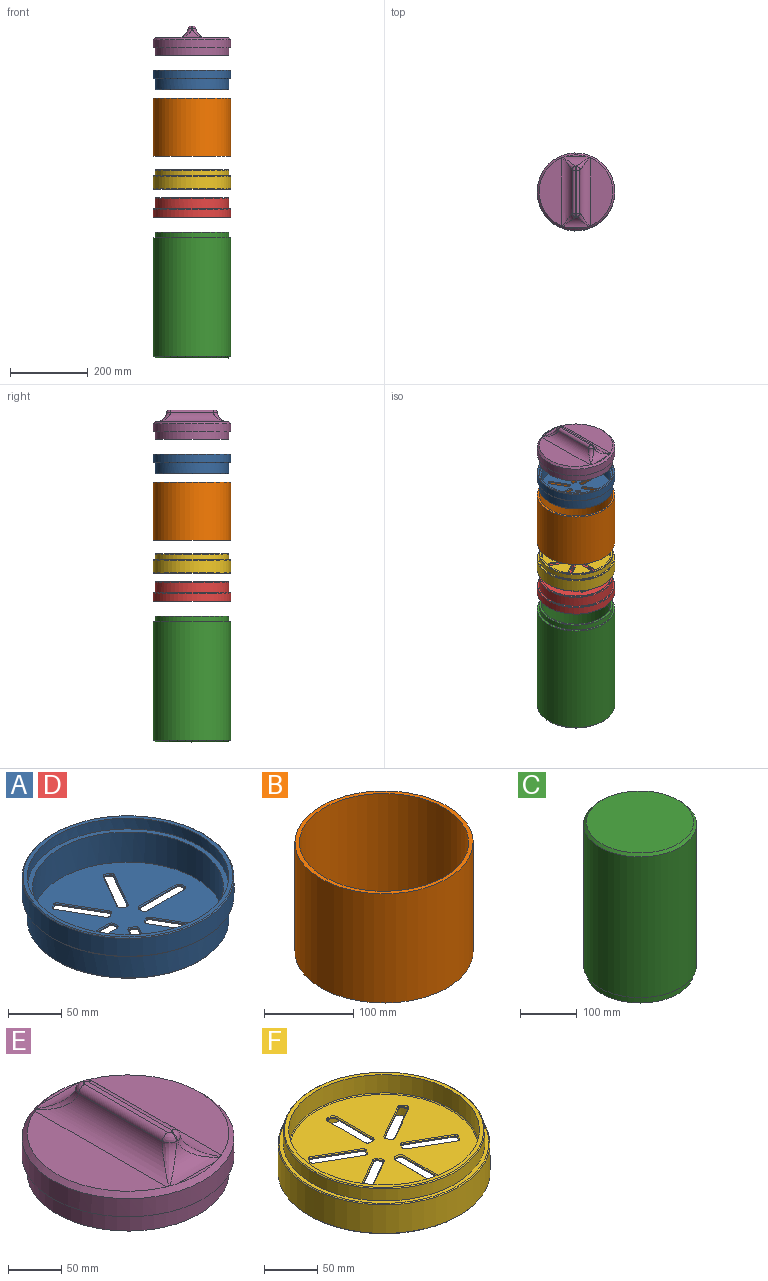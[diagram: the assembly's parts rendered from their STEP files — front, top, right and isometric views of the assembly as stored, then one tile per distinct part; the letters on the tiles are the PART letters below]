
ASSEMBLY  parts=6 mates=5
PART A: 158 faces, bbox 200x200x51.1 mm
  f0: cylinder r=95mm len=190mm, axis (0,0,-1), area 7341.9mm2, adj f1,f154
  f1: plane 198x198mm, normal (0,0,1), area 2437.9mm2, adj f0,f155
  f2: cylinder r=100mm len=200mm, axis (0,0,-1), area 12943.4mm2, adj f155,f156
  f3: plane 198x198mm, normal (0,0,-1), area 2437.9mm2, adj f4,f156
  f4: cylinder r=95mm len=190mm, axis (0,0,1), area 16414.8mm2, adj f3,f157
  f5: plane 42.94x25.37mm, normal (-0.61,-0.35,-0.71), area 69.3mm2, adj f6,f7,f27,f128
  f6: cone r=3mm half-angle=45deg, axis (0,0,-1), area 7.8mm2, adj f5,f8,f28,f128
  f7: cone r=3mm half-angle=45deg, axis (0,0,-1), area 7.8mm2, adj f5,f9,f26,f128
  f8: plane 3.1x2.37mm, normal (-0.35,0.61,-0.71), area 4.2mm2, adj f6,f10,f21,f128
  f9: plane 3.1x2.37mm, normal (0.35,-0.61,-0.71), area 4.2mm2, adj f7,f11,f25,f128
  f10: cone r=3mm half-angle=45deg, axis (0,0,-1), area 7.8mm2, adj f8,f12,f22,f128
  f11: cone r=3mm half-angle=45deg, axis (0,0,-1), area 7.8mm2, adj f9,f12,f24,f128
  f12: plane 42.94x25.37mm, normal (0.61,0.35,-0.71), area 69.3mm2, adj f10,f11,f23,f128
  f13: plane 42.94x25.37mm, normal (-0.61,-0.35,0.71), area 69.3mm2, adj f14,f15,f27,f129
  f14: cone r=3mm half-angle=45deg, axis (0,0,1), area 7.8mm2, adj f13,f16,f26,f129
  f15: cone r=3mm half-angle=45deg, axis (0,0,1), area 7.8mm2, adj f13,f17,f28,f129
  f16: plane 3.1x2.37mm, normal (0.35,-0.61,0.71), area 4.2mm2, adj f14,f18,f25,f129
  f17: plane 3.1x2.37mm, normal (-0.35,0.61,0.71), area 4.2mm2, adj f15,f19,f21,f129
  f18: cone r=3mm half-angle=45deg, axis (0,0,1), area 7.8mm2, adj f16,f20,f24,f129
  f19: cone r=3mm half-angle=45deg, axis (0,0,1), area 7.8mm2, adj f17,f20,f22,f129
  f20: plane 42.94x25.37mm, normal (0.61,0.35,0.71), area 69.3mm2, adj f18,f19,f23,f129
  f21: plane 2.6x1.5mm, normal (-0.5,0.87,0), area 3mm2, adj f8,f17,f22,f28
  f22: cylinder r=3mm len=4.1mm, axis (0,0,-1), area 4.7mm2, adj f10,f19,f21,f23
  f23: plane 42.44x24.5mm, normal (0.87,0.5,0), area 49mm2, adj f12,f20,f22,f24
  f24: cylinder r=3mm len=4.1mm, axis (0,0,-1), area 4.7mm2, adj f11,f18,f23,f25
  f25: plane 2.6x1.5mm, normal (0.5,-0.87,0), area 3mm2, adj f9,f16,f24,f26
  f26: cylinder r=3mm len=4.1mm, axis (0,0,-1), area 4.7mm2, adj f7,f14,f25,f27
  f27: plane 42.44x24.5mm, normal (-0.87,-0.5,0), area 49mm2, adj f5,f13,f26,f28
  f28: cylinder r=3mm len=4.1mm, axis (0,0,-1), area 4.7mm2, adj f6,f15,f21,f27
  f29: plane 42.94x25.37mm, normal (-0.61,0.35,-0.71), area 69.3mm2, adj f30,f31,f51,f128
  f30: cone r=3mm half-angle=45deg, axis (0,0,-1), area 7.8mm2, adj f29,f32,f52,f128
  f31: cone r=3mm half-angle=45deg, axis (0,0,-1), area 7.8mm2, adj f29,f33,f50,f128
  f32: plane 3.1x2.37mm, normal (0.35,0.61,-0.71), area 4.2mm2, adj f30,f34,f45,f128
  f33: plane 3.1x2.37mm, normal (-0.35,-0.61,-0.71), area 4.2mm2, adj f31,f35,f49,f128
  f34: cone r=3mm half-angle=45deg, axis (0,0,-1), area 7.8mm2, adj f32,f36,f46,f128
  f35: cone r=3mm half-angle=45deg, axis (0,0,-1), area 7.8mm2, adj f33,f36,f48,f128
  f36: plane 42.94x25.37mm, normal (0.61,-0.35,-0.71), area 69.3mm2, adj f34,f35,f47,f128
  f37: plane 42.94x25.37mm, normal (-0.61,0.35,0.71), area 69.3mm2, adj f38,f39,f51,f129
  f38: cone r=3mm half-angle=45deg, axis (0,0,1), area 7.8mm2, adj f37,f40,f50,f129
  f39: cone r=3mm half-angle=45deg, axis (0,0,1), area 7.8mm2, adj f37,f41,f52,f129
  f40: plane 3.1x2.37mm, normal (-0.35,-0.61,0.71), area 4.2mm2, adj f38,f42,f49,f129
  f41: plane 3.1x2.37mm, normal (0.35,0.61,0.71), area 4.2mm2, adj f39,f43,f45,f129
  f42: cone r=3mm half-angle=45deg, axis (0,0,1), area 7.8mm2, adj f40,f44,f48,f129
  f43: cone r=3mm half-angle=45deg, axis (0,0,1), area 7.8mm2, adj f41,f44,f46,f129
  f44: plane 42.94x25.37mm, normal (0.61,-0.35,0.71), area 69.3mm2, adj f42,f43,f47,f129
  f45: plane 2.6x1.5mm, normal (0.5,0.87,0), area 3mm2, adj f32,f41,f46,f52
  f46: cylinder r=3mm len=4.1mm, axis (0,0,-1), area 4.7mm2, adj f34,f43,f45,f47
  f47: plane 42.44x24.5mm, normal (0.87,-0.5,0), area 49mm2, adj f36,f44,f46,f48
  f48: cylinder r=3mm len=4.1mm, axis (0,0,-1), area 4.7mm2, adj f35,f42,f47,f49
  f49: plane 2.6x1.5mm, normal (-0.5,-0.87,0), area 3mm2, adj f33,f40,f48,f50
  f50: cylinder r=3mm len=4.1mm, axis (0,0,-1), area 4.7mm2, adj f31,f38,f49,f51
  f51: plane 42.44x24.5mm, normal (-0.87,0.5,0), area 49mm2, adj f29,f37,f50,f52
  f52: cylinder r=3mm len=4.1mm, axis (0,0,-1), area 4.7mm2, adj f30,f39,f45,f51
  f53: plane 49x1mm, normal (0,0.71,-0.71), area 69.3mm2, adj f54,f55,f75,f128
  f54: cone r=3mm half-angle=45deg, axis (0,0,-1), area 7.8mm2, adj f53,f56,f76,f128
  f55: cone r=3mm half-angle=45deg, axis (0,0,-1), area 7.8mm2, adj f53,f57,f74,f128
  f56: plane 3x1mm, normal (0.71,0,-0.71), area 4.2mm2, adj f54,f58,f69,f128
  f57: plane 3x1mm, normal (-0.71,0,-0.71), area 4.2mm2, adj f55,f59,f73,f128
  f58: cone r=3mm half-angle=45deg, axis (0,0,-1), area 7.8mm2, adj f56,f60,f70,f128
  f59: cone r=3mm half-angle=45deg, axis (0,0,-1), area 7.8mm2, adj f57,f60,f72,f128
  f60: plane 49x1mm, normal (0,-0.71,-0.71), area 69.3mm2, adj f58,f59,f71,f128
  f61: plane 49x1mm, normal (0,0.71,0.71), area 69.3mm2, adj f62,f63,f75,f129
  f62: cone r=3mm half-angle=45deg, axis (0,0,1), area 7.8mm2, adj f61,f64,f74,f129
  f63: cone r=3mm half-angle=45deg, axis (0,0,1), area 7.8mm2, adj f61,f65,f76,f129
  f64: plane 3x1mm, normal (-0.71,0,0.71), area 4.2mm2, adj f62,f66,f73,f129
  f65: plane 3x1mm, normal (0.71,0,0.71), area 4.2mm2, adj f63,f67,f69,f129
  f66: cone r=3mm half-angle=45deg, axis (0,0,1), area 7.8mm2, adj f64,f68,f72,f129
  f67: cone r=3mm half-angle=45deg, axis (0,0,1), area 7.8mm2, adj f65,f68,f70,f129
  f68: plane 49x1mm, normal (0,-0.71,0.71), area 69.3mm2, adj f66,f67,f71,f129
  f69: plane 3x1mm, normal (1,0,0), area 3mm2, adj f56,f65,f70,f76
  f70: cylinder r=3mm len=3mm, axis (0,0,-1), area 4.7mm2, adj f58,f67,f69,f71
  f71: plane 49x1mm, normal (0,-1,0), area 49mm2, adj f60,f68,f70,f72
  f72: cylinder r=3mm len=3mm, axis (0,0,-1), area 4.7mm2, adj f59,f66,f71,f73
  f73: plane 3x1mm, normal (-1,0,0), area 3mm2, adj f57,f64,f72,f74
  f74: cylinder r=3mm len=3mm, axis (0,0,-1), area 4.7mm2, adj f55,f62,f73,f75
  f75: plane 49x1mm, normal (0,1,0), area 49mm2, adj f53,f61,f74,f76
  f76: cylinder r=3mm len=3mm, axis (0,0,-1), area 4.7mm2, adj f54,f63,f69,f75
  f77: plane 42.94x25.37mm, normal (0.61,0.35,-0.71), area 69.3mm2, adj f78,f79,f99,f128
  f78: cone r=3mm half-angle=45deg, axis (0,0,-1), area 7.8mm2, adj f77,f80,f100,f128
  f79: cone r=3mm half-angle=45deg, axis (0,0,-1), area 7.8mm2, adj f77,f81,f98,f128
  f80: plane 3.1x2.37mm, normal (0.35,-0.61,-0.71), area 4.2mm2, adj f78,f82,f93,f128
  f81: plane 3.1x2.37mm, normal (-0.35,0.61,-0.71), area 4.2mm2, adj f79,f83,f97,f128
  f82: cone r=3mm half-angle=45deg, axis (0,0,-1), area 7.8mm2, adj f80,f84,f94,f128
  f83: cone r=3mm half-angle=45deg, axis (0,0,-1), area 7.8mm2, adj f81,f84,f96,f128
  f84: plane 42.94x25.37mm, normal (-0.61,-0.35,-0.71), area 69.3mm2, adj f82,f83,f95,f128
  f85: plane 42.94x25.37mm, normal (0.61,0.35,0.71), area 69.3mm2, adj f86,f87,f99,f129
  f86: cone r=3mm half-angle=45deg, axis (0,0,1), area 7.8mm2, adj f85,f88,f98,f129
  f87: cone r=3mm half-angle=45deg, axis (0,0,1), area 7.8mm2, adj f85,f89,f100,f129
  f88: plane 3.1x2.37mm, normal (-0.35,0.61,0.71), area 4.2mm2, adj f86,f90,f97,f129
  f89: plane 3.1x2.37mm, normal (0.35,-0.61,0.71), area 4.2mm2, adj f87,f91,f93,f129
  f90: cone r=3mm half-angle=45deg, axis (0,0,1), area 7.8mm2, adj f88,f92,f96,f129
  f91: cone r=3mm half-angle=45deg, axis (0,0,1), area 7.8mm2, adj f89,f92,f94,f129
  f92: plane 42.94x25.37mm, normal (-0.61,-0.35,0.71), area 69.3mm2, adj f90,f91,f95,f129
  f93: plane 2.6x1.5mm, normal (0.5,-0.87,0), area 3mm2, adj f80,f89,f94,f100
  f94: cylinder r=3mm len=4.1mm, axis (0,0,-1), area 4.7mm2, adj f82,f91,f93,f95
  f95: plane 42.44x24.5mm, normal (-0.87,-0.5,0), area 49mm2, adj f84,f92,f94,f96
  f96: cylinder r=3mm len=4.1mm, axis (0,0,-1), area 4.7mm2, adj f83,f90,f95,f97
  f97: plane 2.6x1.5mm, normal (-0.5,0.87,0), area 3mm2, adj f81,f88,f96,f98
  f98: cylinder r=3mm len=4.1mm, axis (0,0,-1), area 4.7mm2, adj f79,f86,f97,f99
  f99: plane 42.44x24.5mm, normal (0.87,0.5,0), area 49mm2, adj f77,f85,f98,f100
  f100: cylinder r=3mm len=4.1mm, axis (0,0,-1), area 4.7mm2, adj f78,f87,f93,f99
  f101: plane 42.94x25.37mm, normal (0.61,-0.35,-0.71), area 69.3mm2, adj f102,f103,f123,f128
  f102: cone r=3mm half-angle=45deg, axis (0,0,-1), area 7.8mm2, adj f101,f104,f124,f128
  f103: cone r=3mm half-angle=45deg, axis (0,0,-1), area 7.8mm2, adj f101,f105,f122,f128
  f104: plane 3.1x2.37mm, normal (-0.35,-0.61,-0.71), area 4.2mm2, adj f102,f106,f117,f128
  f105: plane 3.1x2.37mm, normal (0.35,0.61,-0.71), area 4.2mm2, adj f103,f107,f121,f128
  f106: cone r=3mm half-angle=45deg, axis (0,0,-1), area 7.8mm2, adj f104,f108,f118,f128
  f107: cone r=3mm half-angle=45deg, axis (0,0,-1), area 7.8mm2, adj f105,f108,f120,f128
  f108: plane 42.94x25.37mm, normal (-0.61,0.35,-0.71), area 69.3mm2, adj f106,f107,f119,f128
  f109: plane 42.94x25.37mm, normal (0.61,-0.35,0.71), area 69.3mm2, adj f110,f111,f123,f129
  f110: cone r=3mm half-angle=45deg, axis (0,0,1), area 7.8mm2, adj f109,f112,f122,f129
  f111: cone r=3mm half-angle=45deg, axis (0,0,1), area 7.8mm2, adj f109,f113,f124,f129
  f112: plane 3.1x2.37mm, normal (0.35,0.61,0.71), area 4.2mm2, adj f110,f114,f121,f129
  f113: plane 3.1x2.37mm, normal (-0.35,-0.61,0.71), area 4.2mm2, adj f111,f115,f117,f129
  f114: cone r=3mm half-angle=45deg, axis (0,0,1), area 7.8mm2, adj f112,f116,f120,f129
  f115: cone r=3mm half-angle=45deg, axis (0,0,1), area 7.8mm2, adj f113,f116,f118,f129
  f116: plane 42.94x25.37mm, normal (-0.61,0.35,0.71), area 69.3mm2, adj f114,f115,f119,f129
  f117: plane 2.6x1.5mm, normal (-0.5,-0.87,0), area 3mm2, adj f104,f113,f118,f124
  f118: cylinder r=3mm len=4.1mm, axis (0,0,-1), area 4.7mm2, adj f106,f115,f117,f119
  f119: plane 42.44x24.5mm, normal (-0.87,0.5,0), area 49mm2, adj f108,f116,f118,f120
  f120: cylinder r=3mm len=4.1mm, axis (0,0,-1), area 4.7mm2, adj f107,f114,f119,f121
  f121: plane 2.6x1.5mm, normal (0.5,0.87,0), area 3mm2, adj f105,f112,f120,f122
  f122: cylinder r=3mm len=4.1mm, axis (0,0,-1), area 4.7mm2, adj f103,f110,f121,f123
  f123: plane 42.44x24.5mm, normal (0.87,-0.5,0), area 49mm2, adj f101,f109,f122,f124
  f124: cylinder r=3mm len=4.1mm, axis (0,0,-1), area 4.7mm2, adj f102,f111,f117,f123
  f125: cylinder r=90mm len=180mm, axis (0,0,1), area 565.5mm2, adj f127,f128
  f126: cylinder r=90mm len=180mm, axis (0,0,1), area 19678.9mm2, adj f129,f154
  f127: plane 188x188mm, normal (0,0,-1), area 2312.2mm2, adj f125,f157
  f128: plane 180x180mm, normal (0,0,-1), area 21767.3mm2, adj f5,f6,f7,f8,f9,f10,f11,f12
  f129: plane 180x180mm, normal (0,0,1), area 21767.3mm2, adj f13,f14,f15,f16,f17,f18,f19,f20
  f130: plane 3x1mm, normal (1,0,0), area 3mm2, adj f131,f137,f141,f150
  f131: cylinder r=3mm len=3mm, axis (0,0,-1), area 4.7mm2, adj f130,f132,f139,f148
  f132: plane 49x1mm, normal (0,-1,0), area 49mm2, adj f131,f133,f138,f146
  f133: cylinder r=3mm len=3mm, axis (0,0,-1), area 4.7mm2, adj f132,f134,f140,f147
  f134: plane 3x1mm, normal (-1,0,0), area 3mm2, adj f133,f135,f142,f149
  f135: cylinder r=3mm len=3mm, axis (0,0,-1), area 4.7mm2, adj f134,f136,f144,f151
  f136: plane 49x1mm, normal (0,1,0), area 49mm2, adj f135,f137,f145,f153
  f137: cylinder r=3mm len=3mm, axis (0,0,-1), area 4.7mm2, adj f130,f136,f143,f152
  f138: plane 49x1mm, normal (0,-0.71,0.71), area 69.3mm2, adj f129,f132,f139,f140
  f139: cone r=3mm half-angle=45deg, axis (0,0,1), area 7.8mm2, adj f129,f131,f138,f141
  f140: cone r=3mm half-angle=45deg, axis (0,0,1), area 7.8mm2, adj f129,f133,f138,f142
  f141: plane 3x1mm, normal (0.71,0,0.71), area 4.2mm2, adj f129,f130,f139,f143
  f142: plane 3x1mm, normal (-0.71,0,0.71), area 4.2mm2, adj f129,f134,f140,f144
  f143: cone r=3mm half-angle=45deg, axis (0,0,1), area 7.8mm2, adj f129,f137,f141,f145
  f144: cone r=3mm half-angle=45deg, axis (0,0,1), area 7.8mm2, adj f129,f135,f142,f145
  f145: plane 49x1mm, normal (0,0.71,0.71), area 69.3mm2, adj f129,f136,f143,f144
  f146: plane 49x1mm, normal (0,-0.71,-0.71), area 69.3mm2, adj f128,f132,f147,f148
  f147: cone r=3mm half-angle=45deg, axis (0,0,-1), area 7.8mm2, adj f128,f133,f146,f149
  f148: cone r=3mm half-angle=45deg, axis (0,0,-1), area 7.8mm2, adj f128,f131,f146,f150
  f149: plane 3x1mm, normal (-0.71,0,-0.71), area 4.2mm2, adj f128,f134,f147,f151
  f150: plane 3x1mm, normal (0.71,0,-0.71), area 4.2mm2, adj f128,f130,f148,f152
  f151: cone r=3mm half-angle=45deg, axis (0,0,-1), area 7.8mm2, adj f128,f135,f149,f153
  f152: cone r=3mm half-angle=45deg, axis (0,0,-1), area 7.8mm2, adj f128,f137,f150,f153
  f153: plane 49x1mm, normal (0,0.71,-0.71), area 69.3mm2, adj f128,f136,f151,f152
  f154: plane 190x190mm, normal (0,0,1), area 2906mm2, adj f0,f126
  f155: cone r=99mm half-angle=45deg, axis (0,0,-1), area 884.1mm2, adj f1,f2
  f156: cone r=100mm half-angle=45deg, axis (0,0,1), area 884.1mm2, adj f2,f3
  f157: cone r=95mm half-angle=45deg, axis (0,0,1), area 839.7mm2, adj f4,f127
PART B: 4 faces, bbox 200x200x150 mm
  f0: cylinder r=95mm len=190mm, axis (0,0,-1), area 89535.4mm2, adj f2,f3
  f1: cylinder r=100mm len=200mm, axis (0,0,-1), area 94247.8mm2, adj f2,f3
  f2: plane 200x200mm, normal (0,0,1), area 3063.1mm2, adj f0,f1
  f3: plane 200x200mm, normal (0,0,-1), area 3063.1mm2, adj f0,f1
PART C: 10 faces, bbox 200x200x325 mm
  f0: cylinder r=95mm len=190mm, axis (0,0,1), area 8953.5mm2, adj f3,f6
  f1: cylinder r=95mm len=290mm, axis (0,0,-1), area 173101.8mm2, adj f4,f5
  f2: cylinder r=90mm len=180mm, axis (0,0,1), area 16964.6mm2, adj f3,f4
  f3: plane 190x190mm, normal (0,0,-1), area 2906mm2, adj f0,f2
  f4: plane 190x190mm, normal (0,0,1), area 2906mm2, adj f1,f2
  f5: plane 190x190mm, normal (0,0,-1), area 28352.9mm2, adj f1
  f6: plane 200x200mm, normal (0,0,-1), area 3063.1mm2, adj f0,f9
  f7: plane 190x190mm, normal (0,0,1), area 28352.9mm2, adj f8
  f8: cone r=95mm half-angle=45deg, axis (0,0,-1), area 4331.8mm2, adj f7,f9
  f9: cylinder r=100mm len=305mm, axis (0,0,-1), area 191637.2mm2, adj f6,f8
PART D: same geometry as A
PART E: 30 faces, bbox 200x200x76 mm
  f0: plane 50.69x3.44mm, normal (0,0,1), area 116.8mm2, adj f12,f17
  f1: plane 175.37x58.44mm, normal (0,0,1), area 7406.2mm2, adj f12,f15
  f2: plane 50.69x3.44mm, normal (0,0,1), area 116.8mm2, adj f12,f14
  f3: plane 175.37x58.44mm, normal (0,0,1), area 7406.2mm2, adj f12,f16
  f4: cylinder r=95mm len=190mm, axis (0,0,-1), area 6565.9mm2, adj f10,f11
  f5: cylinder r=100mm len=200mm, axis (0,0,-1), area 13194.7mm2, adj f6,f12
  f6: plane 200x200mm, normal (0,0,-1), area 3063.1mm2, adj f5,f7
  f7: cylinder r=95mm len=190mm, axis (0,0,1), area 11938.1mm2, adj f6,f9
  f8: cylinder r=90mm len=180mm, axis (0,0,1), area 16964.6mm2, adj f9,f10
  f9: plane 190x190mm, normal (0,0,-1), area 2906mm2, adj f7,f8
  f10: plane 190x190mm, normal (0,0,1), area 2906mm2, adj f4,f8
  f11: plane 190x190mm, normal (0,0,-1), area 28352.9mm2, adj f4
  f12: cone r=95mm half-angle=45deg, axis (0,0,-1), area 4336.3mm2, adj f0,f1,f2,f3,f5,f14,f15,f16
  f13: plane 115.09x5.09mm, normal (0,0,1), area 582.2mm2, adj f22,f23,f24,f25,f26,f27,f28,f29
  f14: cylinder r=26.56mm len=66mm, axis (-1,0,0), area 1094.3mm2, adj f2,f12,f18,f21,f25
  f15: cylinder r=26.56mm len=176.97mm, axis (0,-1,0), area 5337.6mm2, adj f1,f12,f18,f19,f29
  f16: cylinder r=26.56mm len=176.97mm, axis (0,1,0), area 5337.6mm2, adj f3,f12,f20,f21,f22
  f17: cylinder r=26.56mm len=66mm, axis (1,0,0), area 1094.3mm2, adj f0,f12,f19,f20,f26
  f18: bspline ~36.16x36.16mm, area 410.2mm2, adj f12,f14,f15,f27
  f19: bspline ~36.16x36.16mm, area 410.2mm2, adj f12,f15,f17,f28
  f20: bspline ~36.16x36.16mm, area 410.2mm2, adj f12,f16,f17,f24
  f21: bspline ~36.16x36.16mm, area 410.2mm2, adj f12,f14,f16,f23
  f22: cylinder r=7.73mm len=111.25mm, axis (0,1,0), area 1242.4mm2, adj f13,f16,f23,f24
  f23: bspline ~10.64x10.11mm, area 111.5mm2, adj f13,f21,f22,f25
  f24: bspline ~10.64x10.11mm, area 111.5mm2, adj f13,f20,f22,f26
  f25: cylinder r=7.73mm len=7.67mm, axis (-1,0,0), area 14mm2, adj f13,f14,f23,f27
  f26: cylinder r=7.73mm len=7.67mm, axis (1,0,0), area 14mm2, adj f13,f17,f24,f28
  f27: bspline ~10.64x10.11mm, area 111.5mm2, adj f13,f18,f25,f29
  f28: bspline ~10.64x10.11mm, area 111.5mm2, adj f13,f19,f26,f29
  f29: cylinder r=7.73mm len=111.25mm, axis (0,-1,0), area 1242.4mm2, adj f13,f15,f27,f28
PART F: 158 faces, bbox 200x200x50 mm
  f0: plane 2.6x1.5mm, normal (-0.87,0.5,0), area 3mm2, adj f1,f7,f59,f104
  f1: cylinder r=3mm len=4.1mm, axis (0,0,1), area 4.7mm2, adj f0,f2,f61,f105
  f2: plane 42.44x24.5mm, normal (-0.5,-0.87,0), area 49mm2, adj f1,f3,f63,f107
  f3: cylinder r=3mm len=4.1mm, axis (0,0,1), area 4.7mm2, adj f2,f4,f62,f109
  f4: plane 2.6x1.5mm, normal (0.87,-0.5,0), area 3mm2, adj f3,f5,f60,f111
  f5: cylinder r=3mm len=4.1mm, axis (0,0,1), area 4.7mm2, adj f4,f6,f58,f110
  f6: plane 42.44x24.5mm, normal (0.5,0.87,0), area 49mm2, adj f5,f7,f56,f108
  f7: cylinder r=3mm len=4.1mm, axis (0,0,1), area 4.7mm2, adj f0,f6,f57,f106
  f8: plane 2.6x1.5mm, normal (-0.87,-0.5,0), area 3mm2, adj f9,f15,f99,f112
  f9: cylinder r=3mm len=4.1mm, axis (0,0,1), area 4.7mm2, adj f8,f10,f101,f113
  f10: plane 42.44x24.5mm, normal (0.5,-0.87,0), area 49mm2, adj f9,f11,f103,f115
  f11: cylinder r=3mm len=4.1mm, axis (0,0,1), area 4.7mm2, adj f10,f12,f102,f117
  f12: plane 2.6x1.5mm, normal (0.87,0.5,0), area 3mm2, adj f11,f13,f100,f119
  f13: cylinder r=3mm len=4.1mm, axis (0,0,1), area 4.7mm2, adj f12,f14,f98,f118
  f14: plane 42.44x24.5mm, normal (-0.5,0.87,0), area 49mm2, adj f13,f15,f96,f116
  f15: cylinder r=3mm len=4.1mm, axis (0,0,1), area 4.7mm2, adj f8,f14,f97,f114
  f16: plane 3x1mm, normal (0,-1,0), area 3mm2, adj f17,f23,f91,f123
  f17: cylinder r=3mm len=3mm, axis (0,0,1), area 4.7mm2, adj f16,f18,f89,f125
  f18: plane 49x1mm, normal (1,0,0), area 49mm2, adj f17,f19,f88,f127
  f19: cylinder r=3mm len=3mm, axis (0,0,1), area 4.7mm2, adj f18,f20,f90,f126
  f20: plane 3x1mm, normal (0,1,0), area 3mm2, adj f19,f21,f92,f124
  f21: cylinder r=3mm len=3mm, axis (0,0,1), area 4.7mm2, adj f20,f22,f94,f122
  f22: plane 49x1mm, normal (-1,0,0), area 49mm2, adj f21,f23,f95,f120
  f23: cylinder r=3mm len=3mm, axis (0,0,1), area 4.7mm2, adj f16,f22,f93,f121
  f24: plane 2.6x1.5mm, normal (0.87,-0.5,0), area 3mm2, adj f25,f31,f83,f131
  f25: cylinder r=3mm len=4.1mm, axis (0,0,1), area 4.7mm2, adj f24,f26,f81,f133
  f26: plane 42.44x24.5mm, normal (0.5,0.87,0), area 49mm2, adj f25,f27,f80,f135
  f27: cylinder r=3mm len=4.1mm, axis (0,0,1), area 4.7mm2, adj f26,f28,f82,f134
  f28: plane 2.6x1.5mm, normal (-0.87,0.5,0), area 3mm2, adj f27,f29,f84,f132
  f29: cylinder r=3mm len=4.1mm, axis (0,0,1), area 4.7mm2, adj f28,f30,f86,f130
  f30: plane 42.44x24.5mm, normal (-0.5,-0.87,0), area 49mm2, adj f29,f31,f87,f128
  f31: cylinder r=3mm len=4.1mm, axis (0,0,1), area 4.7mm2, adj f24,f30,f85,f129
  f32: plane 2.6x1.5mm, normal (0.87,0.5,0), area 3mm2, adj f33,f39,f75,f139
  f33: cylinder r=3mm len=4.1mm, axis (0,0,1), area 4.7mm2, adj f32,f34,f73,f141
  f34: plane 42.44x24.5mm, normal (-0.5,0.87,0), area 49mm2, adj f33,f35,f72,f143
  f35: cylinder r=3mm len=4.1mm, axis (0,0,1), area 4.7mm2, adj f34,f36,f74,f142
  f36: plane 2.6x1.5mm, normal (-0.87,-0.5,0), area 3mm2, adj f35,f37,f76,f140
  f37: cylinder r=3mm len=4.1mm, axis (0,0,1), area 4.7mm2, adj f36,f38,f78,f138
  f38: plane 42.44x24.5mm, normal (0.5,-0.87,0), area 49mm2, adj f37,f39,f79,f136
  f39: cylinder r=3mm len=4.1mm, axis (0,0,1), area 4.7mm2, adj f32,f38,f77,f137
  f40: plane 188x188mm, normal (0,0,-1), area 24079.5mm2, adj f56,f57,f58,f59,f60,f61,f62,f63
  f41: cylinder r=100mm len=200mm, axis (0,0,-1), area 20734.5mm2, adj f155,f157
  f42: plane 198x198mm, normal (0,0,1), area 2437.9mm2, adj f44,f157
  f43: cylinder r=90mm len=180mm, axis (0,0,-1), area 11875.2mm2, adj f45,f152
  f44: cylinder r=95mm len=190mm, axis (0,0,-1), area 8356.6mm2, adj f42,f156
  f45: plane 188x188mm, normal (0,0,1), area 2312.2mm2, adj f43,f156
  f46: cylinder r=95mm len=190mm, axis (0,0,1), area 14325.7mm2, adj f153,f154
  f47: plane 178x178mm, normal (0,0,1), area 21205mm2, adj f104,f105,f106,f107,f108,f109,f110,f111
  f48: plane 3x1mm, normal (0,-1,0), area 3mm2, adj f49,f55,f71,f148
  f49: cylinder r=3mm len=3mm, axis (0,0,1), area 4.7mm2, adj f48,f50,f70,f150
  f50: plane 49x1mm, normal (1,0,0), area 49mm2, adj f49,f51,f68,f151
  f51: cylinder r=3mm len=3mm, axis (0,0,1), area 4.7mm2, adj f50,f52,f66,f149
  f52: plane 3x1mm, normal (0,1,0), area 3mm2, adj f51,f53,f64,f147
  f53: cylinder r=3mm len=3mm, axis (0,0,1), area 4.7mm2, adj f52,f54,f65,f145
  f54: plane 49x1mm, normal (-1,0,0), area 49mm2, adj f53,f55,f67,f144
  f55: cylinder r=3mm len=3mm, axis (0,0,1), area 4.7mm2, adj f48,f54,f69,f146
  f56: plane 42.94x25.37mm, normal (0.35,0.61,-0.71), area 69.3mm2, adj f6,f40,f57,f58
  f57: cone r=4mm half-angle=45deg, axis (0,0,-1), area 7.8mm2, adj f7,f40,f56,f59
  f58: cone r=4mm half-angle=45deg, axis (0,0,-1), area 7.8mm2, adj f5,f40,f56,f60
  f59: plane 3.1x2.37mm, normal (-0.61,0.35,-0.71), area 4.2mm2, adj f0,f40,f57,f61
  f60: plane 3.1x2.37mm, normal (0.61,-0.35,-0.71), area 4.2mm2, adj f4,f40,f58,f62
  f61: cone r=4mm half-angle=45deg, axis (0,0,-1), area 7.8mm2, adj f1,f40,f59,f63
  f62: cone r=4mm half-angle=45deg, axis (0,0,-1), area 7.8mm2, adj f3,f40,f60,f63
  f63: plane 42.94x25.37mm, normal (-0.35,-0.61,-0.71), area 69.3mm2, adj f2,f40,f61,f62
  f64: plane 3x1mm, normal (0,0.71,-0.71), area 4.2mm2, adj f40,f52,f65,f66
  f65: cone r=4mm half-angle=45deg, axis (0,0,-1), area 7.8mm2, adj f40,f53,f64,f67
  f66: cone r=4mm half-angle=45deg, axis (0,0,-1), area 7.8mm2, adj f40,f51,f64,f68
  f67: plane 49x1mm, normal (-0.71,0,-0.71), area 69.3mm2, adj f40,f54,f65,f69
  f68: plane 49x1mm, normal (0.71,0,-0.71), area 69.3mm2, adj f40,f50,f66,f70
  f69: cone r=4mm half-angle=45deg, axis (0,0,-1), area 7.8mm2, adj f40,f55,f67,f71
  f70: cone r=4mm half-angle=45deg, axis (0,0,-1), area 7.8mm2, adj f40,f49,f68,f71
  f71: plane 3x1mm, normal (0,-0.71,-0.71), area 4.2mm2, adj f40,f48,f69,f70
  f72: plane 42.94x25.37mm, normal (-0.35,0.61,-0.71), area 69.3mm2, adj f34,f40,f73,f74
  f73: cone r=4mm half-angle=45deg, axis (0,0,-1), area 7.8mm2, adj f33,f40,f72,f75
  f74: cone r=4mm half-angle=45deg, axis (0,0,-1), area 7.8mm2, adj f35,f40,f72,f76
  f75: plane 3.1x2.37mm, normal (0.61,0.35,-0.71), area 4.2mm2, adj f32,f40,f73,f77
  f76: plane 3.1x2.37mm, normal (-0.61,-0.35,-0.71), area 4.2mm2, adj f36,f40,f74,f78
  f77: cone r=4mm half-angle=45deg, axis (0,0,-1), area 7.8mm2, adj f39,f40,f75,f79
  f78: cone r=4mm half-angle=45deg, axis (0,0,-1), area 7.8mm2, adj f37,f40,f76,f79
  f79: plane 42.94x25.37mm, normal (0.35,-0.61,-0.71), area 69.3mm2, adj f38,f40,f77,f78
  f80: plane 42.94x25.37mm, normal (0.35,0.61,-0.71), area 69.3mm2, adj f26,f40,f81,f82
  f81: cone r=4mm half-angle=45deg, axis (0,0,-1), area 7.8mm2, adj f25,f40,f80,f83
  f82: cone r=4mm half-angle=45deg, axis (0,0,-1), area 7.8mm2, adj f27,f40,f80,f84
  f83: plane 3.1x2.37mm, normal (0.61,-0.35,-0.71), area 4.2mm2, adj f24,f40,f81,f85
  f84: plane 3.1x2.37mm, normal (-0.61,0.35,-0.71), area 4.2mm2, adj f28,f40,f82,f86
  f85: cone r=4mm half-angle=45deg, axis (0,0,-1), area 7.8mm2, adj f31,f40,f83,f87
  f86: cone r=4mm half-angle=45deg, axis (0,0,-1), area 7.8mm2, adj f29,f40,f84,f87
  f87: plane 42.94x25.37mm, normal (-0.35,-0.61,-0.71), area 69.3mm2, adj f30,f40,f85,f86
  f88: plane 49x1mm, normal (0.71,0,-0.71), area 69.3mm2, adj f18,f40,f89,f90
  f89: cone r=4mm half-angle=45deg, axis (0,0,-1), area 7.8mm2, adj f17,f40,f88,f91
  f90: cone r=4mm half-angle=45deg, axis (0,0,-1), area 7.8mm2, adj f19,f40,f88,f92
  f91: plane 3x1mm, normal (0,-0.71,-0.71), area 4.2mm2, adj f16,f40,f89,f93
  f92: plane 3x1mm, normal (0,0.71,-0.71), area 4.2mm2, adj f20,f40,f90,f94
  f93: cone r=4mm half-angle=45deg, axis (0,0,-1), area 7.8mm2, adj f23,f40,f91,f95
  f94: cone r=4mm half-angle=45deg, axis (0,0,-1), area 7.8mm2, adj f21,f40,f92,f95
  f95: plane 49x1mm, normal (-0.71,0,-0.71), area 69.3mm2, adj f22,f40,f93,f94
  f96: plane 42.94x25.37mm, normal (-0.35,0.61,-0.71), area 69.3mm2, adj f14,f40,f97,f98
  f97: cone r=4mm half-angle=45deg, axis (0,0,-1), area 7.8mm2, adj f15,f40,f96,f99
  f98: cone r=4mm half-angle=45deg, axis (0,0,-1), area 7.8mm2, adj f13,f40,f96,f100
  f99: plane 3.1x2.37mm, normal (-0.61,-0.35,-0.71), area 4.2mm2, adj f8,f40,f97,f101
  f100: plane 3.1x2.37mm, normal (0.61,0.35,-0.71), area 4.2mm2, adj f12,f40,f98,f102
  f101: cone r=4mm half-angle=45deg, axis (0,0,-1), area 7.8mm2, adj f9,f40,f99,f103
  f102: cone r=4mm half-angle=45deg, axis (0,0,-1), area 7.8mm2, adj f11,f40,f100,f103
  f103: plane 42.94x25.37mm, normal (0.35,-0.61,-0.71), area 69.3mm2, adj f10,f40,f101,f102
  f104: plane 3.1x2.37mm, normal (-0.61,0.35,0.71), area 4.2mm2, adj f0,f47,f105,f106
  f105: cone r=3mm half-angle=45deg, axis (0,0,1), area 7.8mm2, adj f1,f47,f104,f107
  f106: cone r=3mm half-angle=45deg, axis (0,0,1), area 7.8mm2, adj f7,f47,f104,f108
  f107: plane 42.94x25.37mm, normal (-0.35,-0.61,0.71), area 69.3mm2, adj f2,f47,f105,f109
  f108: plane 42.94x25.37mm, normal (0.35,0.61,0.71), area 69.3mm2, adj f6,f47,f106,f110
  f109: cone r=3mm half-angle=45deg, axis (0,0,1), area 7.8mm2, adj f3,f47,f107,f111
  f110: cone r=3mm half-angle=45deg, axis (0,0,1), area 7.8mm2, adj f5,f47,f108,f111
  f111: plane 3.1x2.37mm, normal (0.61,-0.35,0.71), area 4.2mm2, adj f4,f47,f109,f110
  f112: plane 3.1x2.37mm, normal (-0.61,-0.35,0.71), area 4.2mm2, adj f8,f47,f113,f114
  f113: cone r=3mm half-angle=45deg, axis (0,0,1), area 7.8mm2, adj f9,f47,f112,f115
  f114: cone r=3mm half-angle=45deg, axis (0,0,1), area 7.8mm2, adj f15,f47,f112,f116
  f115: plane 42.94x25.37mm, normal (0.35,-0.61,0.71), area 69.3mm2, adj f10,f47,f113,f117
  f116: plane 42.94x25.37mm, normal (-0.35,0.61,0.71), area 69.3mm2, adj f14,f47,f114,f118
  f117: cone r=3mm half-angle=45deg, axis (0,0,1), area 7.8mm2, adj f11,f47,f115,f119
  f118: cone r=3mm half-angle=45deg, axis (0,0,1), area 7.8mm2, adj f13,f47,f116,f119
  f119: plane 3.1x2.37mm, normal (0.61,0.35,0.71), area 4.2mm2, adj f12,f47,f117,f118
  f120: plane 49x1mm, normal (-0.71,0,0.71), area 69.3mm2, adj f22,f47,f121,f122
  f121: cone r=3mm half-angle=45deg, axis (0,0,1), area 7.8mm2, adj f23,f47,f120,f123
  f122: cone r=3mm half-angle=45deg, axis (0,0,1), area 7.8mm2, adj f21,f47,f120,f124
  f123: plane 3x1mm, normal (0,-0.71,0.71), area 4.2mm2, adj f16,f47,f121,f125
  f124: plane 3x1mm, normal (0,0.71,0.71), area 4.2mm2, adj f20,f47,f122,f126
  f125: cone r=3mm half-angle=45deg, axis (0,0,1), area 7.8mm2, adj f17,f47,f123,f127
  f126: cone r=3mm half-angle=45deg, axis (0,0,1), area 7.8mm2, adj f19,f47,f124,f127
  f127: plane 49x1mm, normal (0.71,0,0.71), area 69.3mm2, adj f18,f47,f125,f126
  f128: plane 42.94x25.37mm, normal (-0.35,-0.61,0.71), area 69.3mm2, adj f30,f47,f129,f130
  f129: cone r=3mm half-angle=45deg, axis (0,0,1), area 7.8mm2, adj f31,f47,f128,f131
  f130: cone r=3mm half-angle=45deg, axis (0,0,1), area 7.8mm2, adj f29,f47,f128,f132
  f131: plane 3.1x2.37mm, normal (0.61,-0.35,0.71), area 4.2mm2, adj f24,f47,f129,f133
  f132: plane 3.1x2.37mm, normal (-0.61,0.35,0.71), area 4.2mm2, adj f28,f47,f130,f134
  f133: cone r=3mm half-angle=45deg, axis (0,0,1), area 7.8mm2, adj f25,f47,f131,f135
  f134: cone r=3mm half-angle=45deg, axis (0,0,1), area 7.8mm2, adj f27,f47,f132,f135
  f135: plane 42.94x25.37mm, normal (0.35,0.61,0.71), area 69.3mm2, adj f26,f47,f133,f134
  f136: plane 42.94x25.37mm, normal (0.35,-0.61,0.71), area 69.3mm2, adj f38,f47,f137,f138
  f137: cone r=3mm half-angle=45deg, axis (0,0,1), area 7.8mm2, adj f39,f47,f136,f139
  f138: cone r=3mm half-angle=45deg, axis (0,0,1), area 7.8mm2, adj f37,f47,f136,f140
  f139: plane 3.1x2.37mm, normal (0.61,0.35,0.71), area 4.2mm2, adj f32,f47,f137,f141
  f140: plane 3.1x2.37mm, normal (-0.61,-0.35,0.71), area 4.2mm2, adj f36,f47,f138,f142
  f141: cone r=3mm half-angle=45deg, axis (0,0,1), area 7.8mm2, adj f33,f47,f139,f143
  f142: cone r=3mm half-angle=45deg, axis (0,0,1), area 7.8mm2, adj f35,f47,f140,f143
  f143: plane 42.94x25.37mm, normal (-0.35,0.61,0.71), area 69.3mm2, adj f34,f47,f141,f142
  f144: plane 49x1mm, normal (-0.71,0,0.71), area 69.3mm2, adj f47,f54,f145,f146
  f145: cone r=3mm half-angle=45deg, axis (0,0,1), area 7.8mm2, adj f47,f53,f144,f147
  f146: cone r=3mm half-angle=45deg, axis (0,0,1), area 7.8mm2, adj f47,f55,f144,f148
  f147: plane 3x1mm, normal (0,0.71,0.71), area 4.2mm2, adj f47,f52,f145,f149
  f148: plane 3x1mm, normal (0,-0.71,0.71), area 4.2mm2, adj f47,f48,f146,f150
  f149: cone r=3mm half-angle=45deg, axis (0,0,1), area 7.8mm2, adj f47,f51,f147,f151
  f150: cone r=3mm half-angle=45deg, axis (0,0,1), area 7.8mm2, adj f47,f49,f148,f151
  f151: plane 49x1mm, normal (0.71,0,0.71), area 69.3mm2, adj f47,f50,f149,f150
  f152: cone r=89mm half-angle=45deg, axis (0,0,1), area 795.3mm2, adj f43,f47
  f153: cone r=95mm half-angle=45deg, axis (0,0,-1), area 839.7mm2, adj f40,f46
  f154: plane 198x198mm, normal (0,0,-1), area 2437.9mm2, adj f46,f155
  f155: cone r=100mm half-angle=45deg, axis (0,0,1), area 884.1mm2, adj f41,f154
  f156: cone r=94mm half-angle=45deg, axis (0,0,-1), area 839.7mm2, adj f44,f45
  f157: cone r=99mm half-angle=45deg, axis (0,0,-1), area 884.1mm2, adj f41,f42
PLACE A t=(-131.41,51.35,242.33)mm
PLACE B rot(axis=(0,0.12,0.99),0deg) t=(-131.41,51.35,69.83)mm
PLACE C rot(axis=(-1,0,0),180deg) t=(-131.41,51.35,-145.47)mm
PLACE D rot(axis=(0,-1,0),180deg) t=(-131.41,51.35,-37.67)mm
PLACE E t=(-131.41,51.35,350.13)mm
PLACE F rot(axis=(0,0.12,0.99),0deg) t=(-131.41,51.35,9.83)mm
MATE fastened D.f0 <-> F.f44  axis (0,0,1) through (-131.41,51.35,-65.17)mm
MATE fastened B.f0 <-> A.f0  axis (0,0,1) through (-131.41,51.35,219.83)mm
MATE fastened E.f4 <-> A.f125  axis (0,0,-1) through (-131.41,51.35,330.13)mm
MATE fastened F.f44 <-> B.f0  axis (0,0,1) through (-131.41,51.35,19.83)mm
MATE fastened C.f0 <-> D.f125  axis (0,0,1) through (-131.41,51.35,-125.47)mm
